# Revit family: Hager-Gamma-IP30-syst-FR-fr
name_source: partatom
category: Electrical Equipment
units: mm (PartAtom-declared; Revit-internal decimal feet)

## family parameters
Cut with Voids When Loaded = No
Host = Face
Panel Configuration = Two Columns, Circuits Across
Part Type = Panelboard
Room Calculation Point = No
Round Connector Dimension = Use Diameter
Shared = No

## types (10) — shared parameters
EF000003 - mode de pose = EV000384 - saillie
EF000049 - profondeur = 103 mm  [stored 0.337927 ft]
EF000116 - numéro RAL = 9010
EF001062 - finition CEM = No
EF001596 - matériau du boîtier/corps = EV000139 - plastique
EF006306 - avec serrure = No
HG000001 - nombre de colonnes = 1
HG000002 - avec porte = No
HG000003 - Gamme = Gamma
HG000005 - Epaisseur = 3 mm  [stored 0.00984252 ft]
HG000006 - Encastré = No
HG000009 - Porte à double battant = No
HG000010 - Portes asymétriques = No
HG000011 - Rangées du bas vides = No
HG000017 - Distance entre pôles = 18 mm  [stored 0.0590551 ft]
Manufacturer = Hager
Type Comments = Gamma
zero-valued in all types: Default Elevation, EF000332 - hauteur d'encastrement, EF000846 - largeur d'encastrement, HG000007 - Nombre de colonnes vides, HG000008 - Nombre de rangées vides

## per-type parameters (varying)
| type | EF000007 - couleur | EF000008 - largeur | EF000040 - hauteur | EF000118 - avec cadre/support de montage | EF000218 - profondeur d'encastrement | EF000266 - nombre de rangées | EF000339 - type de capot | EF001088 - possibilité de montage en saillie | EF001131 - profondeur intérieure | EF001134 - rail DIN | EF002950 - largeur en nombre de modules | EF004462 - type de fermeture | EF005474 - indice de protection (IP) | EF006244 - couvercle/porte transparent(e) | EF009212 - finition du couvercle | EF015776 - borne de mise à la terre | EF015777 - borne à conducteur neutre | EF015941 - porte pour transmission du signal | HG000004 - Référence fabricant | Model |
| Saillie IP30 L250 H250 P103 13 Modules - GD113A |  | 250 mm  [stored 0.82021 ft] | 250 mm  [stored 0.82021 ft] | No | 0 mm  [stored 0 ft] | 1 |  | No | 0 mm  [stored 0 ft] | No | 13 | EV000154 - autre | EV006410 - IP30 | No |  | Yes | Yes | Yes | GD113A | GD113A |
| Saillie IP30 L250 H375 P103 13 Modules - GD213A |  | 250 mm  [stored 0.82021 ft] | 375 mm | No | 0 mm  [stored 0 ft] | 2 | EV001012 - couvercle | No | 0 mm  [stored 0 ft] | No | 13 |  | EV006410 - IP30 | No |  | No | No | No | GD213A | GD213A |
| Saillie IP30 L250 H500 P103 13 Modules - GD313A |  | 250 mm  [stored 0.82021 ft] | 500 mm  [stored 1.64042 ft] | No | 0 mm  [stored 0 ft] | 3 | EV001012 - couvercle | No | 0 mm  [stored 0 ft] | No | 13 | EV000154 - autre | EV006410 - IP30 | No |  | No | No | No | GD313A | GD313A |
| Saillie IP30 L250 H625 P103 13 Modules - GD413A |  | 250 mm  [stored 0.82021 ft] | 625 mm  [stored 2.05052 ft] | No | 0 mm  [stored 0 ft] | 4 | EV001012 - couvercle | No | 0 mm  [stored 0 ft] | No | 13 | EV000154 - autre | EV006410 - IP30 | No |  | No | No | No | GD413A | GD413A |
| Saillie IP30 L355 H250 P103 10 Modules - GD018E | EV000202 - blanc | 355 mm  [stored 1.1647 ft] | 250 mm  [stored 0.82021 ft] | No | 103 mm  [stored 0.337927 ft] | 0 | EV001012 - couvercle | Yes | 55 mm | No | 10 | EV000154 - autre | EV006410 - IP30 | Yes | EV009916 - avec échancrure | No | No | No | GD018E | GD018E |
| Saillie IP30 L355 H250 P103 18 Modules - GD118A | EV000202 - blanc | 355 mm  [stored 1.1647 ft] | 250 mm  [stored 0.82021 ft] | Yes | 0 mm  [stored 0 ft] | 1 | EV001012 - couvercle | Yes | 103 mm  [stored 0.337927 ft] | Yes | 18 | EV000154 - autre | EV006410 - IP30 | No | EV009916 - avec échancrure | No | No | No | GD118A | GD118A |
| Saillie IP30 L355 H375 P103 18 Modules - GD218A | EV000202 - blanc | 355 mm  [stored 1.1647 ft] | 375 mm | Yes | 0 mm  [stored 0 ft] | 2 | EV001012 - couvercle | Yes | 103 mm  [stored 0.337927 ft] | Yes | 18 | EV000154 - autre | EV006410 - IP30 | No | EV009916 - avec échancrure | No | No | No | GD218A | GD218A |
| Saillie IP30 L355 H500 P103 18 Modules - GD318A | EV000202 - blanc | 355 mm  [stored 1.1647 ft] | 500 mm  [stored 1.64042 ft] | Yes | 0 mm  [stored 0 ft] | 3 | EV001012 - couvercle | Yes | 103 mm  [stored 0.337927 ft] | Yes | 18 | EV000154 - autre | EV006410 - IP30 | No | EV009916 - avec échancrure | No | No | No | GD318A | GD318A |
| Saillie IP30 L355 H625 P103 18 Modules - GD418A | EV000202 - blanc | 355 mm  [stored 1.1647 ft] | 625 mm  [stored 2.05052 ft] | Yes | 0 mm  [stored 0 ft] | 4 | EV001012 - couvercle | Yes | 103 mm  [stored 0.337927 ft] | Yes | 18 | EV000154 - autre | EV006410 - IP30 | No | EV009916 - avec échancrure | No | No | No | GD418A | GD418A |
| Saillie IP40 L355 H250 P103 10 Modules - GD018A |  | 355 mm  [stored 1.1647 ft] | 250 mm  [stored 0.82021 ft] | No | 0 mm  [stored 0 ft] | 1 | EV001012 - couvercle | No | 0 mm  [stored 0 ft] | No | 10 | EV000154 - autre | EV006415 - IP40 | No |  | No | No | No | GD018A | GD018A |

note: [stored X ft] marks values corroborated as IEEE doubles in the binary element streams (Revit-internal decimal feet)

## geometry (parser evidence)
native form markers: Sweep x17
no freeform markers — native parametric forms only
